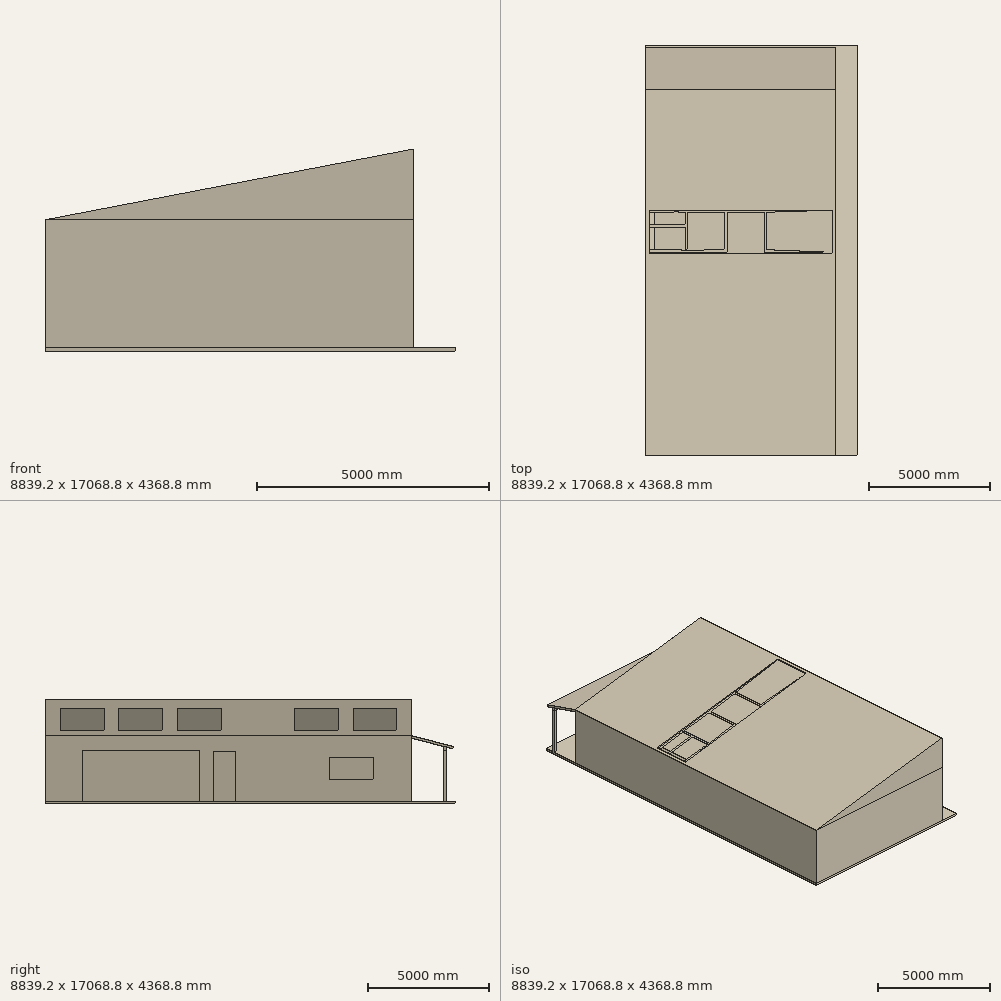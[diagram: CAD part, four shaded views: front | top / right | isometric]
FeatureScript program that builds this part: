
annotation { "Feature Type Name" : "Feature", "Feature Type Description" : "" }
export const myFeature = defineFeature(function(context is Context, id is Id, definition is map)
    precondition{}
    {
        {
            var Q0;
            Q0=qCreatedBy(makeId("Top.planeOp"),FACE);
            var sketch = newSketch(context, id + "F0", { "sketchPlane" : qUnion([Q0])});
            skLineSegment(sketch, "E0", {"start": v(0, 0) * mm, "end": v(0, 15240) * mm});
            skLineSegment(sketch, "E1", {"start": v(0, 15240) * mm, "end": v(7924.8, 15240) * mm});
            skLineSegment(sketch, "E2", {"start": v(7924.8, 15240) * mm, "end": v(7924.8, 0) * mm});
            skLineSegment(sketch, "E3", {"start": v(0, 0) * mm, "end": v(7924.8, 0) * mm});
            skLineSegment(sketch, "E4", {"start": v(152.4, 152.4) * mm, "end": v(152.4, 15087.6) * mm});
            skLineSegment(sketch, "E5", {"start": v(7772.4, 15087.6) * mm, "end": v(7772.4, 152.4) * mm});
            skLineSegment(sketch, "E6.trimOffspring", {"start": v(152.4, 15087.6) * mm, "end": v(7772.4, 15087.6) * mm});
            skLineSegment(sketch, "E7", {"start": v(152.4, 152.4) * mm, "end": v(7772.4, 152.4) * mm});
            skSolve(sketch);
        }
        {
            var Q0;
            Q0=qCreatedBy(makeId("Top.planeOp"),FACE);
            var sketch = newSketch(context, id + "F1", { "sketchPlane" : qUnion([Q0])});
            skLineSegment(sketch, "E8.bottom", {"start": v(0, 0) * mm, "end": v(8839.2, 0) * mm});
            skLineSegment(sketch, "E8.top", {"start": v(0, 17068.8) * mm, "end": v(8839.2, 17068.8) * mm});
            skLineSegment(sketch, "E8.left", {"start": v(0, 0) * mm, "end": v(0, 17068.8) * mm});
            skLineSegment(sketch, "E8.right", {"start": v(8839.2, 0) * mm, "end": v(8839.2, 17068.8) * mm});
            skSolve(sketch);
        }
        {
            var Q0;
            Q0=makeQuery(id+"F1.imprint","IMPRINT",FACE,{"disambiguationData":[TD([[makeQuery(id+"F1.imprint","IMPRINT",EDGE,{"derivedFrom":sQuery(id+"F1.wireOp",EDGE,"E8.bottom")}),1.0]])]});
            extrude(context, id + "F2", {"entities" : qUnion([Q0]), "oppositeDirection" : true, "depth" : 101.6 * mm});
        }
        {
            var Q0;
            Q0=makeQuery(id+"F0.imprint","IMPRINT",FACE,{"disambiguationData":[TD([[makeQuery(id+"F0.imprint","IMPRINT",EDGE,{"derivedFrom":sQuery(id+"F0.wireOp",EDGE,"E0")}),-1.0]])]});
            var Q1;
            Q1=makeQuery(id+"F0.imprint","IMPRINT",FACE,{"disambiguationData":[TD([[makeQuery(id+"F0.imprint","IMPRINT",EDGE,{"derivedFrom":sQuery(id+"F0.wireOp",EDGE,"8d0bd455-d409-4c0b-9b16-9c128ab7819c")}),-1.0]])]});
            var Q2;
            Q2=makeQuery(id+"F0.imprint","IMPRINT",FACE,{"disambiguationData":[TD([[makeQuery(id+"F0.imprint","IMPRINT",EDGE,{"derivedFrom":sQuery(id+"F0.wireOp",EDGE,"E2")}),-1.0]])]});
            extrude(context, id + "F3", {"entities" : qUnion([Q0, Q1, Q2]), "depth" : 2743.2 * mm});
        }
        {
            var Q0;
            Q0=makeQuery(id+"F3.opExtrude","SWEPT_FACE",FACE,{"disambiguationData":[OSD([sQuery(id+"F0.wireOp",EDGE,"E3")])]});
            var sketch = newSketch(context, id + "F4", { "sketchPlane" : qUnion([Q0])});
            skLineSegment(sketch, "E9.0", {"start": v(0, 2743.2) * mm, "end": v(7924.8, 2743.2) * mm});
            skLineSegment(sketch, "E10", {"start": v(7924.8, 2743.2) * mm, "end": v(7924.8, 4267.2) * mm});
            skLineSegment(sketch, "E11", {"start": v(7924.8, 4267.2) * mm, "end": v(0, 2743.2) * mm});
            skSolve(sketch);
        }
        {
            var Q0;
            Q0=makeQuery(id+"F4.imprint","IMPRINT",FACE,{"disambiguationData":[TD([[makeQuery(id+"F4.imprint","IMPRINT",EDGE,{"derivedFrom":sQuery(id+"F4.wireOp",EDGE,"E9.0")}),1.0]])]});
            extrude(context, id + "F5", {"entities" : qUnion([Q0]), "oppositeDirection" : true, "depth" : 15240 * mm});
        }
        {
            var Q0;
            Q0=makeQuery(id+"F3.opExtrude","SWEPT_FACE",FACE,{"disambiguationData":[OSD([sQuery(id+"F0.wireOp",EDGE,"E2")])]});
            var sketch = newSketch(context, id + "F6", { "sketchPlane" : qUnion([Q0])});
            skLineSegment(sketch, "E12.bottom", {"start": v(1524, 0) * mm, "end": v(6400.8, 0) * mm});
            skLineSegment(sketch, "E12.top", {"start": v(1524, 2133.6) * mm, "end": v(6400.8, 2133.6) * mm});
            skLineSegment(sketch, "E12.left", {"start": v(1524, 0) * mm, "end": v(1524, 2133.6) * mm});
            skLineSegment(sketch, "E12.right", {"start": v(6400.8, 0) * mm, "end": v(6400.8, 2133.6) * mm});
            skSolve(sketch);
        }
        {
            var Q0;
            Q0=makeQuery(id+"F6.imprint","IMPRINT",FACE,{"disambiguationData":[TD([[makeQuery(id+"F6.imprint","IMPRINT",EDGE,{"derivedFrom":sQuery(id+"F6.wireOp",EDGE,"E12.bottom")}),-1.0]])]});
            extrude(context, id + "F7", {"entities" : qUnion([Q0]), "operationType" : NewBodyOperationType.REMOVE, "oppositeDirection" : true, "depth" : 304.8 * mm});
        }
        {
            var Q0;
            Q0=makeQuery(id+"F3.opExtrude","SWEPT_FACE",FACE,{"disambiguationData":[OSD([sQuery(id+"F0.wireOp",EDGE,"E2")])]});
            var sketch = newSketch(context, id + "F8", { "sketchPlane" : qUnion([Q0])});
            skLineSegment(sketch, "E13", {"start": v(15240, 2743.2) * mm, "end": v(16988.67, 2286) * mm});
            skLineSegment(sketch, "E14", {"start": v(16988.67, 2286) * mm, "end": v(16988.67, 2180.98) * mm});
            skLineSegment(sketch, "E15", {"start": v(16988.67, 2180.98) * mm, "end": v(15240, 2638.18) * mm});
            skLineSegment(sketch, "E16", {"start": v(15240, 2638.18) * mm, "end": v(15240, 2743.2) * mm});
            skSolve(sketch);
        }
        {
            var Q0;
            Q0=makeQuery(id+"F8.imprint","IMPRINT",FACE,{"disambiguationData":[TD([[makeQuery(id+"F8.imprint","IMPRINT",EDGE,{"derivedFrom":sQuery(id+"F8.wireOp",EDGE,"E13")}),-1.0]])]});
            extrude(context, id + "F9", {"entities" : qUnion([Q0]), "oppositeDirection" : true, "depth" : 7924.8 * mm});
        }
        {
            var Q0;
            Q0=makeQuery(id+"F3.opExtrude","SWEPT_FACE",FACE,{"disambiguationData":[OSD([sQuery(id+"F0.wireOp",EDGE,"E1")])]});
            var sketch = newSketch(context, id + "F10", { "sketchPlane" : qUnion([Q0])});
            skLineSegment(sketch, "E17.bottom", {"start": v(-914.4, 0) * mm, "end": v(-1828.8, 0) * mm});
            skLineSegment(sketch, "E17.top", {"start": v(-914.4, 2032) * mm, "end": v(-1828.8, 2032) * mm});
            skLineSegment(sketch, "E17.left", {"start": v(-914.4, 0) * mm, "end": v(-914.4, 2032) * mm});
            skLineSegment(sketch, "E17.right", {"start": v(-1828.8, 0) * mm, "end": v(-1828.8, 2032) * mm});
            skLineSegment(sketch, "E18.bottom", {"start": v(-7010.4, 0) * mm, "end": v(-6400.8, 0) * mm});
            skLineSegment(sketch, "E18.top", {"start": v(-7010.4, 1524) * mm, "end": v(-6400.8, 1524) * mm});
            skLineSegment(sketch, "E18.left", {"start": v(-7010.4, 0) * mm, "end": v(-7010.4, 1524) * mm});
            skLineSegment(sketch, "E18.right", {"start": v(-6400.8, 0) * mm, "end": v(-6400.8, 1524) * mm});
            skLineSegment(sketch, "E19.bottom", {"start": v(-3048, 1828.8) * mm, "end": v(-4876.8, 1828.8) * mm});
            skLineSegment(sketch, "E19.top", {"start": v(-3048, 914.4) * mm, "end": v(-4876.8, 914.4) * mm});
            skLineSegment(sketch, "E19.left", {"start": v(-3048, 1828.8) * mm, "end": v(-3048, 914.4) * mm});
            skLineSegment(sketch, "E19.right", {"start": v(-4876.8, 1828.8) * mm, "end": v(-4876.8, 914.4) * mm});
            skSolve(sketch);
        }
        {
            var Q0;
            Q0=makeQuery(id+"F10.imprint","IMPRINT",FACE,{"disambiguationData":[TD([[makeQuery(id+"F10.imprint","IMPRINT",EDGE,{"derivedFrom":sQuery(id+"F10.wireOp",EDGE,"E18.bottom")}),-1.0]])]});
            var Q1;
            Q1=makeQuery(id+"F10.imprint","IMPRINT",FACE,{"disambiguationData":[TD([[makeQuery(id+"F10.imprint","IMPRINT",EDGE,{"derivedFrom":sQuery(id+"F10.wireOp",EDGE,"E19.bottom")}),1.0]])]});
            var Q2;
            Q2=makeQuery(id+"F10.imprint","IMPRINT",FACE,{"disambiguationData":[TD([[makeQuery(id+"F10.imprint","IMPRINT",EDGE,{"derivedFrom":sQuery(id+"F10.wireOp",EDGE,"E17.bottom")}),-1.0]])]});
            extrude(context, id + "F11", {"entities" : qUnion([Q0, Q1, Q2]), "operationType" : NewBodyOperationType.REMOVE, "oppositeDirection" : true, "depth" : 304.8 * mm});
        }
        {
            var Q0;
            Q0=makeQuery(id+"F5.opExtrude","SWEPT_FACE",FACE,{"disambiguationData":[OSD([sQuery(id+"F4.wireOp",EDGE,"E9.0")])]});
            shell(context, id + "F12", {"entities" : qUnion([Q0]), "thickness" : 152.4 * mm});
        }
        {
            var Q0;
            Q0=makeQuery(id+"F5.opExtrude","SWEPT_FACE",FACE,{"disambiguationData":[OSD([sQuery(id+"F4.wireOp",EDGE,"E10")])]});
            var sketch = newSketch(context, id + "F13", { "sketchPlane" : qUnion([Q0])});
            skLineSegment(sketch, "E20.bottom", {"start": v(609.6, 3883.89) * mm, "end": v(2438.4, 3883.89) * mm});
            skLineSegment(sketch, "E20.top", {"start": v(609.6, 2969.49) * mm, "end": v(2438.4, 2969.49) * mm});
            skLineSegment(sketch, "E20.left", {"start": v(609.6, 3883.89) * mm, "end": v(609.6, 2969.49) * mm});
            skLineSegment(sketch, "E20.right", {"start": v(2438.4, 3883.89) * mm, "end": v(2438.4, 2969.49) * mm});
            skLineSegment(sketch, "E21.1.0.0", {"start": v(3048, 2969.49) * mm, "end": v(4876.8, 2969.49) * mm});
            skLineSegment(sketch, "E21.1.0.1", {"start": v(3048, 3883.89) * mm, "end": v(4876.8, 3883.89) * mm});
            skLineSegment(sketch, "E21.1.0.2", {"start": v(4876.8, 3883.89) * mm, "end": v(4876.8, 2969.49) * mm});
            skLineSegment(sketch, "E21.1.0.3", {"start": v(3048, 3883.89) * mm, "end": v(3048, 2969.49) * mm});
            skLineSegment(sketch, "E21.2.0.0", {"start": v(5486.4, 2969.49) * mm, "end": v(7315.2, 2969.49) * mm});
            skLineSegment(sketch, "E21.2.0.1", {"start": v(5486.4, 3883.89) * mm, "end": v(7315.2, 3883.89) * mm});
            skLineSegment(sketch, "E21.2.0.2", {"start": v(7315.2, 3883.89) * mm, "end": v(7315.2, 2969.49) * mm});
            skLineSegment(sketch, "E21.2.0.3", {"start": v(5486.4, 3883.89) * mm, "end": v(5486.4, 2969.49) * mm});
            skLineSegment(sketch, "E21.4.0.0", {"start": v(10363.2, 2969.49) * mm, "end": v(12192, 2969.49) * mm});
            skLineSegment(sketch, "E21.4.0.1", {"start": v(10363.2, 3883.89) * mm, "end": v(12192, 3883.89) * mm});
            skLineSegment(sketch, "E21.4.0.2", {"start": v(12192, 3883.89) * mm, "end": v(12192, 2969.49) * mm});
            skLineSegment(sketch, "E21.4.0.3", {"start": v(10363.2, 3883.89) * mm, "end": v(10363.2, 2969.49) * mm});
            skLineSegment(sketch, "E21.5.0.0", {"start": v(12801.6, 2969.49) * mm, "end": v(14630.4, 2969.49) * mm});
            skLineSegment(sketch, "E21.5.0.1", {"start": v(12801.6, 3883.89) * mm, "end": v(14630.4, 3883.89) * mm});
            skLineSegment(sketch, "E21.5.0.2", {"start": v(14630.4, 3883.89) * mm, "end": v(14630.4, 2969.49) * mm});
            skLineSegment(sketch, "E21.5.0.3", {"start": v(12801.6, 3883.89) * mm, "end": v(12801.6, 2969.49) * mm});
            skLineSegment(sketch, "E21.direction1", {"start": v(-21539.37, 2969.49) * mm, "end": v(-19100.97, 2969.49) * mm, "construction": true});
            skSolve(sketch);
        }
        {
            var Q0;
            Q0=makeQuery(id+"F13.imprint","IMPRINT",FACE,{"disambiguationData":[TD([[makeQuery(id+"F13.imprint","IMPRINT",EDGE,{"derivedFrom":sQuery(id+"F13.wireOp",EDGE,"E20.bottom")}),-1.0]])]});
            var Q1;
            Q1=makeQuery(id+"F13.imprint","IMPRINT",FACE,{"disambiguationData":[TD([[makeQuery(id+"F13.imprint","IMPRINT",EDGE,{"derivedFrom":sQuery(id+"F13.wireOp",EDGE,"E21.1.0.0")}),1.0]])]});
            var Q2;
            Q2=makeQuery(id+"F13.imprint","IMPRINT",FACE,{"disambiguationData":[TD([[makeQuery(id+"F13.imprint","IMPRINT",EDGE,{"derivedFrom":sQuery(id+"F13.wireOp",EDGE,"E21.2.0.0")}),1.0]])]});
            var Q3;
            Q3=makeQuery(id+"F13.imprint","IMPRINT",FACE,{"disambiguationData":[TD([[makeQuery(id+"F13.imprint","IMPRINT",EDGE,{"derivedFrom":sQuery(id+"F13.wireOp",EDGE,"E21.3.0.0")}),1.0]])]});
            var Q4;
            Q4=makeQuery(id+"F13.imprint","IMPRINT",FACE,{"disambiguationData":[TD([[makeQuery(id+"F13.imprint","IMPRINT",EDGE,{"derivedFrom":sQuery(id+"F13.wireOp",EDGE,"E21.4.0.0")}),1.0]])]});
            var Q5;
            Q5=makeQuery(id+"F13.imprint","IMPRINT",FACE,{"disambiguationData":[TD([[makeQuery(id+"F13.imprint","IMPRINT",EDGE,{"derivedFrom":sQuery(id+"F13.wireOp",EDGE,"E21.5.0.0")}),1.0]])]});
            extrude(context, id + "F14", {"entities" : qUnion([Q0, Q1, Q2, Q3, Q4, Q5]), "operationType" : NewBodyOperationType.REMOVE, "oppositeDirection" : true, "depth" : 304.8 * mm});
        }
        {
            var Q0;
            Q0=makeQuery(id+"F3.opExtrude","SWEPT_FACE",FACE,{"disambiguationData":[OSD([sQuery(id+"F0.wireOp",EDGE,"E2")])]});
            var sketch = newSketch(context, id + "F15", { "sketchPlane" : qUnion([Q0])});
            skLineSegment(sketch, "E22.bottom", {"start": v(16683.87, 2287.24) * mm, "end": v(16582.27, 2287.24) * mm});
            skLineSegment(sketch, "E22.top", {"start": v(16683.87, 2134.84) * mm, "end": v(16582.27, 2134.84) * mm});
            skLineSegment(sketch, "E22.left", {"start": v(16683.87, 2287.24) * mm, "end": v(16683.87, 2134.84) * mm});
            skLineSegment(sketch, "E22.right", {"start": v(16582.27, 2287.24) * mm, "end": v(16582.27, 2134.84) * mm});
            skSolve(sketch);
        }
        {
            var Q0;
            Q0=makeQuery(id+"F15.imprint","IMPRINT",FACE,{"disambiguationData":[TD([[makeQuery(id+"F15.imprint","IMPRINT",EDGE,{"derivedFrom":sQuery(id+"F15.wireOp",EDGE,"E22.bottom")}),1.0]])]});
            extrude(context, id + "F16", {"entities" : qUnion([Q0]), "oppositeDirection" : true, "depth" : 7924.8 * mm});
        }
        {
            var Q0;
            Q0=makeQuery(id+"F16.opExtrude","SWEPT_FACE",FACE,{"disambiguationData":[OSD([sQuery(id+"F15.wireOp",EDGE,"E22.top")])]});
            var sketch = newSketch(context, id + "F17", { "sketchPlane" : qUnion([Q0])});
            skLineSegment(sketch, "E23", {"start": v(7924.8, -16683.87) * mm, "end": v(7924.8, -16582.27) * mm});
            skLineSegment(sketch, "E24", {"start": v(7924.8, -16582.27) * mm, "end": v(7772.4, -16582.27) * mm});
            skLineSegment(sketch, "E25", {"start": v(7772.4, -16582.27) * mm, "end": v(7772.4, -16683.87) * mm});
            skLineSegment(sketch, "E26", {"start": v(7772.4, -16683.87) * mm, "end": v(7924.8, -16683.87) * mm});
            skLineSegment(sketch, "E27", {"start": v(0, -16582.27) * mm, "end": v(152.4, -16582.27) * mm});
            skLineSegment(sketch, "E28", {"start": v(152.4, -16582.27) * mm, "end": v(152.4, -16683.87) * mm});
            skLineSegment(sketch, "E29", {"start": v(152.4, -16683.87) * mm, "end": v(0, -16683.87) * mm});
            skLineSegment(sketch, "E30", {"start": v(0, -16683.87) * mm, "end": v(0, -16582.27) * mm});
            skLineSegment(sketch, "E31", {"start": v(5334, -16683.87) * mm, "end": v(5334, -16582.27) * mm});
            skLineSegment(sketch, "E32", {"start": v(5334, -16582.27) * mm, "end": v(5181.6, -16582.27) * mm});
            skLineSegment(sketch, "E33", {"start": v(5181.6, -16582.27) * mm, "end": v(5181.6, -16683.87) * mm});
            skLineSegment(sketch, "E34", {"start": v(5181.6, -16683.87) * mm, "end": v(5334, -16683.87) * mm});
            skLineSegment(sketch, "E35", {"start": v(2590.8, -16582.27) * mm, "end": v(2590.8, -16683.87) * mm});
            skLineSegment(sketch, "E36", {"start": v(2590.8, -16683.87) * mm, "end": v(2743.2, -16683.87) * mm});
            skLineSegment(sketch, "E37", {"start": v(2743.2, -16683.87) * mm, "end": v(2743.2, -16582.27) * mm});
            skLineSegment(sketch, "E38", {"start": v(2743.2, -16582.27) * mm, "end": v(2590.8, -16582.27) * mm});
            skSolve(sketch);
        }
        {
            var Q0;
            Q0=makeQuery(id+"F17.imprint","IMPRINT",FACE,{"disambiguationData":[TD([[makeQuery(id+"F17.imprint","IMPRINT",EDGE,{"derivedFrom":sQuery(id+"F17.wireOp",EDGE,"E23")}),1.0]])]});
            var Q1;
            Q1=makeQuery(id+"F17.imprint","IMPRINT",FACE,{"disambiguationData":[TD([[makeQuery(id+"F17.imprint","IMPRINT",EDGE,{"derivedFrom":sQuery(id+"F17.wireOp",EDGE,"E31")}),1.0]])]});
            var Q2;
            Q2=makeQuery(id+"F17.imprint","IMPRINT",FACE,{"disambiguationData":[TD([[makeQuery(id+"F17.imprint","IMPRINT",EDGE,{"derivedFrom":sQuery(id+"F17.wireOp",EDGE,"E35")}),1.0]])]});
            var Q3;
            Q3=makeQuery(id+"F17.imprint","IMPRINT",FACE,{"disambiguationData":[TD([[makeQuery(id+"F17.imprint","IMPRINT",EDGE,{"derivedFrom":sQuery(id+"F17.wireOp",EDGE,"E27")}),-1.0]])]});
            extrude(context, id + "F18", {"entities" : qUnion([Q0, Q1, Q2, Q3]), "depth" : 2209.8 * mm});
        }
        {
            var Q0;
            Q0=qCreatedBy(makeId("Top.planeOp"),FACE);
            var sketch = newSketch(context, id + "F19", { "sketchPlane" : qUnion([Q0])});
            skLineSegment(sketch, "E39.0", {"start": v(152.4, 152.4) * mm, "end": v(152.4, 15087.6) * mm, "construction": true});
            skLineSegment(sketch, "E40.0", {"start": v(7772.4, 15087.6) * mm, "end": v(7772.4, 8572.5) * mm, "construction": true});
            skLineSegment(sketch, "E41.0", {"start": v(152.4, 15087.6) * mm, "end": v(914.4, 15087.6) * mm, "construction": true});
            skLineSegment(sketch, "E42.0", {"start": v(1828.8, 15087.6) * mm, "end": v(6400.8, 15087.6) * mm, "construction": true});
            skLineSegment(sketch, "E43.0", {"start": v(7010.4, 15087.6) * mm, "end": v(7772.4, 15087.6) * mm, "construction": true});
            skLineSegment(sketch, "E44.0", {"start": v(7772.4, 1524) * mm, "end": v(7772.4, 152.4) * mm, "construction": true});
            skLineSegment(sketch, "E45.0", {"start": v(152.4, 152.4) * mm, "end": v(7772.4, 152.4) * mm, "construction": true});
            skLineSegment(sketch, "E46", {"start": v(152.4, 10210.8) * mm, "end": v(7772.4, 10210.8) * mm});
            skLineSegment(sketch, "E47", {"start": v(7772.4, 10210.8) * mm, "end": v(7772.4, 10096.5) * mm});
            skLineSegment(sketch, "E48", {"start": v(152.4, 10096.5) * mm, "end": v(152.4, 10210.8) * mm});
            skLineSegment(sketch, "E49", {"start": v(3314.7, 8572.5) * mm, "end": v(1790.7, 8572.5) * mm});
            skLineSegment(sketch, "E50", {"start": v(152.4, 8572.5) * mm, "end": v(152.4, 8458.2) * mm});
            skLineSegment(sketch, "E51", {"start": v(152.4, 8458.2) * mm, "end": v(3429, 8458.2) * mm});
            skLineSegment(sketch, "E52.trimOffspring", {"start": v(1676.4, 10096.5) * mm, "end": v(152.4, 10096.5) * mm});
            skLineSegment(sketch, "E53", {"start": v(7772.4, 10096.5) * mm, "end": v(5067.3, 10096.5) * mm});
            skLineSegment(sketch, "E54", {"start": v(3429, 10096.5) * mm, "end": v(3429, 8458.2) * mm});
            skLineSegment(sketch, "E55", {"start": v(3314.7, 10096.5) * mm, "end": v(3314.7, 8572.5) * mm});
            skLineSegment(sketch, "E56.trimOffspring", {"start": v(3314.7, 10096.5) * mm, "end": v(1790.7, 10096.5) * mm});
            skLineSegment(sketch, "E57", {"start": v(1790.7, 10096.5) * mm, "end": v(1790.7, 8572.5) * mm});
            skLineSegment(sketch, "E58.trimOffspring", {"start": v(1676.4, 8572.5) * mm, "end": v(152.4, 8572.5) * mm});
            skLineSegment(sketch, "E59", {"start": v(1676.4, 10096.5) * mm, "end": v(1676.4, 9601.2) * mm});
            skLineSegment(sketch, "E60", {"start": v(1676.4, 9486.9) * mm, "end": v(152.4, 9486.9) * mm});
            skLineSegment(sketch, "E61", {"start": v(152.4, 9486.9) * mm, "end": v(152.4, 9601.2) * mm});
            skLineSegment(sketch, "E62", {"start": v(152.4, 9601.2) * mm, "end": v(1676.4, 9601.2) * mm});
            skLineSegment(sketch, "E63.trimOffspring", {"start": v(1676.4, 9486.9) * mm, "end": v(1676.4, 8572.5) * mm});
            skLineSegment(sketch, "E64", {"start": v(4953, 10096.5) * mm, "end": v(4953, 8458.2) * mm});
            skLineSegment(sketch, "E65", {"start": v(4953, 8458.2) * mm, "end": v(7772.4, 8458.2) * mm});
            skLineSegment(sketch, "E66", {"start": v(7772.4, 8572.5) * mm, "end": v(5067.3, 8572.5) * mm});
            skLineSegment(sketch, "E67", {"start": v(5067.3, 8572.5) * mm, "end": v(5067.3, 10096.5) * mm});
            skLineSegment(sketch, "E68.trimOffspring", {"start": v(4953, 10096.5) * mm, "end": v(3429, 10096.5) * mm});
            skLineSegment(sketch, "E69.trimOffspring", {"start": v(7772.4, 8458.2) * mm, "end": v(7772.4, 6400.8) * mm, "construction": true});
            skLineSegment(sketch, "E70", {"start": v(7772.4, 8458.2) * mm, "end": v(7772.4, 8572.5) * mm});
            skSolve(sketch);
        }
        {
            var Q0;
            Q0=makeQuery(id+"F19.imprint","IMPRINT",FACE,{"disambiguationData":[TD([[makeQuery(id+"F19.imprint","IMPRINT",EDGE,{"derivedFrom":sQuery(id+"F19.wireOp",EDGE,"E46")}),-1.0]])]});
            extrude(context, id + "F20", {"entities" : qUnion([Q0]), "depth" : 4267.2 * mm});
        }
        {
            var Q0;
            Q0=makeQuery(id+"F20.opExtrude","SWEPT_FACE",FACE,{"disambiguationData":[OSD([sQuery(id+"F19.wireOp",EDGE,"E51")])]});
            var sketch = newSketch(context, id + "F21", { "sketchPlane" : qUnion([Q0])});
            skLineSegment(sketch, "E71.bottom", {"start": v(1219.2, 0) * mm, "end": v(457.2, 0) * mm});
            skLineSegment(sketch, "E71.top", {"start": v(1219.2, 2082.8) * mm, "end": v(457.2, 2082.8) * mm});
            skLineSegment(sketch, "E71.left", {"start": v(1219.2, 0) * mm, "end": v(1219.2, 2082.8) * mm});
            skLineSegment(sketch, "E71.right", {"start": v(457.2, 0) * mm, "end": v(457.2, 2082.8) * mm});
            skLineSegment(sketch, "E72.0", {"start": v(3314.7, 4267.2) * mm, "end": v(3314.7, 0) * mm, "construction": true});
            skSolve(sketch);
        }
        {
            var Q0;
            Q0=makeQuery(id+"F21.imprint","IMPRINT",FACE,{"disambiguationData":[TD([[makeQuery(id+"F21.imprint","IMPRINT",EDGE,{"derivedFrom":sQuery(id+"F21.wireOp",EDGE,"E71.bottom")}),1.0]])]});
            var Q1;
            Q1=makeQuery(id+"F21.imprint","IMPRINT",FACE,{"disambiguationData":[TD([[makeQuery(id+"F21.imprint","IMPRINT",EDGE,{"derivedFrom":sQuery(id+"F21.wireOp",EDGE,"2a17754f-dac8-4a43-9d40-98902cbfab01.bottom")}),1.0]])]});
            extrude(context, id + "F22", {"entities" : qUnion([Q0, Q1]), "operationType" : NewBodyOperationType.REMOVE, "oppositeDirection" : true, "depth" : 152.4 * mm});
        }
        {
            var Q0;
            Q0=makeQuery(id+"F20.opExtrude","SWEPT_FACE",FACE,{"disambiguationData":[OSD([sQuery(id+"F19.wireOp",EDGE,"E46")])]});
            var sketch = newSketch(context, id + "F23", { "sketchPlane" : qUnion([Q0])});
            skLineSegment(sketch, "E73.0", {"start": v(-1219.2, 2082.8) * mm, "end": v(-457.2, 2082.8) * mm});
            skLineSegment(sketch, "E74.0", {"start": v(-457.2, 0) * mm, "end": v(-457.2, 2082.8) * mm});
            skLineSegment(sketch, "E75.0", {"start": v(-1219.2, 0) * mm, "end": v(-1219.2, 2082.8) * mm});
            skLineSegment(sketch, "E76", {"start": v(-1219.2, 0) * mm, "end": v(-457.2, 0) * mm});
            skLineSegment(sketch, "E77.bottom", {"start": v(-3733.8, 0) * mm, "end": v(-4648.2, 0) * mm});
            skLineSegment(sketch, "E77.top", {"start": v(-3733.8, 2082.8) * mm, "end": v(-4648.2, 2082.8) * mm});
            skLineSegment(sketch, "E77.left", {"start": v(-3733.8, 0) * mm, "end": v(-3733.8, 2082.8) * mm});
            skLineSegment(sketch, "E77.right", {"start": v(-4648.2, 0) * mm, "end": v(-4648.2, 2082.8) * mm});
            skLineSegment(sketch, "E78.0", {"start": v(-3429, 4267.2) * mm, "end": v(-3429, 0) * mm, "construction": true});
            skLineSegment(sketch, "E79.bottom", {"start": v(-5372.1, 0) * mm, "end": v(-6134.1, 0) * mm});
            skLineSegment(sketch, "E79.top", {"start": v(-5372.1, 2082.8) * mm, "end": v(-6134.1, 2082.8) * mm});
            skLineSegment(sketch, "E79.left", {"start": v(-5372.1, 0) * mm, "end": v(-5372.1, 2082.8) * mm});
            skLineSegment(sketch, "E79.right", {"start": v(-6134.1, 0) * mm, "end": v(-6134.1, 2082.8) * mm});
            skLineSegment(sketch, "E80.0", {"start": v(-5067.3, 4267.2) * mm, "end": v(-5067.3, 0) * mm, "construction": true});
            skSolve(sketch);
        }
        {
            var Q0;
            Q0=makeQuery(id+"F23.imprint","IMPRINT",FACE,{"disambiguationData":[TD([[makeQuery(id+"F23.imprint","IMPRINT",EDGE,{"derivedFrom":sQuery(id+"F23.wireOp",EDGE,"E73.0")}),-1.0]])]});
            var Q1;
            Q1=makeQuery(id+"F23.imprint","IMPRINT",FACE,{"disambiguationData":[TD([[makeQuery(id+"F23.imprint","IMPRINT",EDGE,{"derivedFrom":sQuery(id+"F23.wireOp",EDGE,"E77.bottom")}),-1.0]])]});
            var Q2;
            Q2=makeQuery(id+"F23.imprint","IMPRINT",FACE,{"disambiguationData":[TD([[makeQuery(id+"F23.imprint","IMPRINT",EDGE,{"derivedFrom":sQuery(id+"F23.wireOp",EDGE,"E79.bottom")}),-1.0]])]});
            extrude(context, id + "F24", {"entities" : qUnion([Q0, Q1, Q2]), "operationType" : NewBodyOperationType.REMOVE, "oppositeDirection" : true, "depth" : 152.4 * mm});
        }
        {
            var Q0;
            Q0=makeQuery(id+"F3.opExtrude","SWEPT_FACE",FACE,{"disambiguationData":[OSD([sQuery(id+"F0.wireOp",EDGE,"E2")])]});
            var sketch = newSketch(context, id + "F25", { "sketchPlane" : qUnion([Q0])});
            skLineSegment(sketch, "E81.bottom", {"start": v(11811, 914.4) * mm, "end": v(13639.8, 914.4) * mm});
            skLineSegment(sketch, "E81.top", {"start": v(11811, 1828.8) * mm, "end": v(13639.8, 1828.8) * mm});
            skLineSegment(sketch, "E81.left", {"start": v(11811, 914.4) * mm, "end": v(11811, 1828.8) * mm});
            skLineSegment(sketch, "E81.right", {"start": v(13639.8, 914.4) * mm, "end": v(13639.8, 1828.8) * mm});
            skLineSegment(sketch, "E82.0", {"start": v(10210.8, 4267.2) * mm, "end": v(10210.8, 0) * mm, "construction": true});
            skSolve(sketch);
        }
        {
            var Q0;
            Q0=makeQuery(id+"F25.imprint","IMPRINT",FACE,{"disambiguationData":[TD([[makeQuery(id+"F25.imprint","IMPRINT",EDGE,{"derivedFrom":sQuery(id+"F25.wireOp",EDGE,"E81.bottom")}),1.0]])]});
            extrude(context, id + "F26", {"entities" : qUnion([Q0]), "operationType" : NewBodyOperationType.REMOVE, "oppositeDirection" : true, "depth" : 152.4 * mm});
        }
        {
            var Q0;
            Q0=makeQuery(id+"F20.opExtrude","SWEPT_FACE",FACE,{"disambiguationData":[OSD([sQuery(id+"F19.wireOp",EDGE,"E46")])]});
            var sketch = newSketch(context, id + "F27", { "sketchPlane" : qUnion([Q0])});
            skLineSegment(sketch, "E83", {"start": v(-8023.64, 4241.7) * mm, "end": v(156.5, 2641.7) * mm});
            skLineSegment(sketch, "E84", {"start": v(156.5, 2641.7) * mm, "end": v(0, 4407.46) * mm});
            skLineSegment(sketch, "E85", {"start": v(0, 4407.46) * mm, "end": v(-8066.88, 4407.46) * mm});
            skLineSegment(sketch, "E86", {"start": v(-8066.88, 4407.46) * mm, "end": v(-8023.64, 4241.7) * mm});
            skSolve(sketch);
        }
        {
            var Q0;
            {var subQ0=sQuery(id+"F27.wireOp",EDGE,"b3c08452-8ef6-4e56-bae7-a6d7a6c5bf9b");Q0=makeQuery(id+"F27.imprint","IMPRINT",FACE,{"disambiguationData":[TD([[makeQuery(id+"F27.imprint","IMPRINT",EDGE,{"derivedFrom":subQ0}),1.0]])]});}
            var Q1;
            {var subQ1=sQuery(id+"F19.wireOp",EDGE,"E46");var subQ6=makeQuery(id+"F20.opExtrude","CAP_EDGE",EDGE,{"disambiguationData":[OSD([subQ1])],"isStart":false});Q1=makeQuery(id+"F27.imprint","IMPRINT",FACE,{"disambiguationData":[TD([[makeQuery(id+"F27.imprint","IMPRINT",EDGE,{"derivedFrom":subQ6}),1.0]])]});}
            var Q2;
            {var subQ0=sQuery(id+"F27.wireOp",EDGE,"0801604d-2e88-4e90-a509-b49f511efdfc");Q2=makeQuery(id+"F27.imprint","IMPRINT",FACE,{"disambiguationData":[TD([[makeQuery(id+"F27.imprint","IMPRINT",EDGE,{"derivedFrom":subQ0}),1.0]])]});}
            var Q3;
            {var subQ0=sQuery(id+"F27.wireOp",EDGE,"332e8762-cf30-4631-aa70-c4558194e265.0");var subQ1=sQuery(id+"F19.wireOp",EDGE,"E46");var subQ2=makeQuery(id+"F20.opExtrude","SWEPT_EDGE",EDGE,{"disambiguationData":[OSD([subQ1,sQuery(id+"F19.wireOp",EDGE,"E47")])]});var subQ3=makeQuery(id+"F27.imprint","INTERSECT",VERTEX,{"derivedFrom":[subQ2,subQ0]});Q3=makeQuery(id+"F27.imprint","IMPRINT",FACE,{"disambiguationData":[TD([[makeQuery(id+"F27.imprint","IMPRINT",EDGE,{"disambiguationData":[TD([[subQ3,-1.0]])],"derivedFrom":subQ0}),-1.0]])]});}
            var Q4;
            {var subQ0=sQuery(id+"F27.wireOp",EDGE,"af90a3a4-edf9-40e9-95e2-4d0e3f2a0b4b");Q4=makeQuery(id+"F27.imprint","IMPRINT",FACE,{"disambiguationData":[TD([[makeQuery(id+"F27.imprint","IMPRINT",EDGE,{"derivedFrom":subQ0}),1.0]])]});}
            extrude(context, id + "F28", {"entities" : qUnion([Q0, Q1, Q2, Q3, Q4]), "operationType" : NewBodyOperationType.REMOVE, "oppositeDirection" : true, "depth" : 1811.8 * mm});
        }
        {
            var Q0;
            Q0=makeQuery(id+"F3.opExtrude","SWEPT_FACE",FACE,{"disambiguationData":[OSD([sQuery(id+"F0.wireOp",EDGE,"E2")])]});
            var sketch = newSketch(context, id + "F29", { "sketchPlane" : qUnion([Q0])});
            skLineSegment(sketch, "E87.bottom", {"start": v(7924.8, 0) * mm, "end": v(7010.4, 0) * mm});
            skLineSegment(sketch, "E87.top", {"start": v(7924.8, 2082.8) * mm, "end": v(7010.4, 2082.8) * mm});
            skLineSegment(sketch, "E87.left", {"start": v(7924.8, 0) * mm, "end": v(7924.8, 2082.8) * mm});
            skLineSegment(sketch, "E87.right", {"start": v(7010.4, 0) * mm, "end": v(7010.4, 2082.8) * mm});
            skSolve(sketch);
        }
        {
            var Q0;
            Q0=makeQuery(id+"F29.imprint","IMPRINT",FACE,{"disambiguationData":[TD([[makeQuery(id+"F29.imprint","IMPRINT",EDGE,{"derivedFrom":sQuery(id+"F29.wireOp",EDGE,"E87.bottom")}),-1.0]])]});
            extrude(context, id + "F30", {"entities" : qUnion([Q0]), "operationType" : NewBodyOperationType.REMOVE, "oppositeDirection" : true, "depth" : 152.4 * mm});
        }
        {
            var Q0;
            Q0=makeQuery(id+"F20.opExtrude","SWEPT_FACE",FACE,{"disambiguationData":[OSD([sQuery(id+"F19.wireOp",EDGE,"E54")])]});
            var sketch = newSketch(context, id + "F31", { "sketchPlane" : qUnion([Q0])});
            skLineSegment(sketch, "E88.bottom", {"start": v(8610.6, 0) * mm, "end": v(9372.6, 0) * mm});
            skLineSegment(sketch, "E88.top", {"start": v(8610.6, 2082.8) * mm, "end": v(9372.6, 2082.8) * mm});
            skLineSegment(sketch, "E88.left", {"start": v(8610.6, 0) * mm, "end": v(8610.6, 2082.8) * mm});
            skLineSegment(sketch, "E88.right", {"start": v(9372.6, 0) * mm, "end": v(9372.6, 2082.8) * mm});
            skSolve(sketch);
        }
        {
            var Q0;
            Q0=makeQuery(id+"F31.imprint","IMPRINT",FACE,{"disambiguationData":[TD([[makeQuery(id+"F31.imprint","IMPRINT",EDGE,{"derivedFrom":sQuery(id+"F31.wireOp",EDGE,"E88.bottom")}),-1.0]])]});
            extrude(context, id + "F32", {"entities" : qUnion([Q0]), "operationType" : NewBodyOperationType.REMOVE, "oppositeDirection" : true, "depth" : 152.4 * mm});
        }
    });
